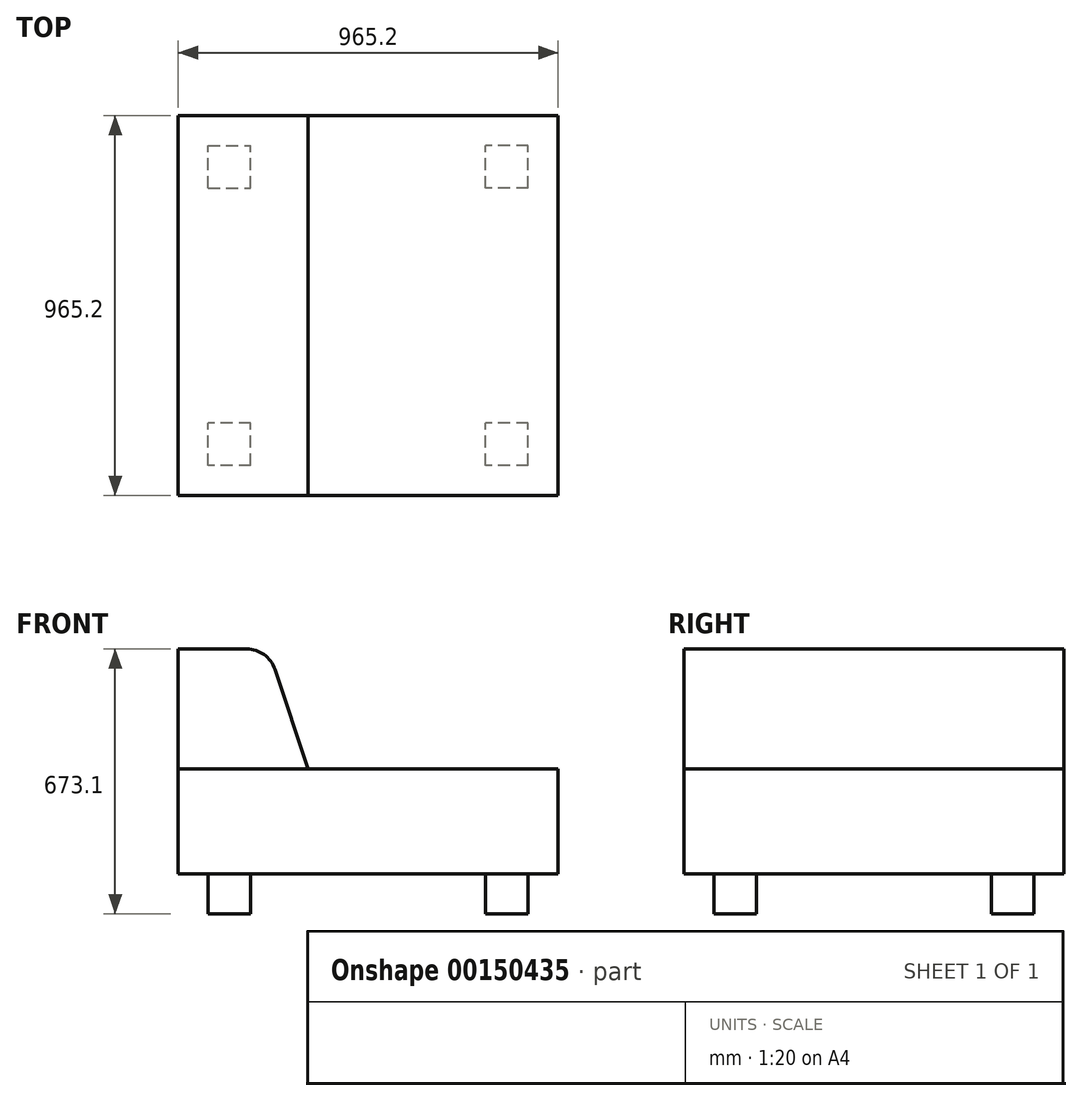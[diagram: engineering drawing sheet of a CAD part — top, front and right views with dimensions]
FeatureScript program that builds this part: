
annotation { "Feature Type Name" : "Feature", "Feature Type Description" : "" }
export const myFeature = defineFeature(function(context is Context, id is Id, definition is map)
    precondition{}
    {
        {
            var Q0;
            Q0=qCreatedBy(makeId("Top.planeOp"),FACE);
            var sketch = newSketch(context, id + "F0", { "sketchPlane" : qUnion([Q0])});
            skLineSegment(sketch, "E0.bottom", {"start": v(482.6, 482.6) * mm, "end": v(-482.6, 482.6) * mm});
            skLineSegment(sketch, "E0.top", {"start": v(482.6, -482.6) * mm, "end": v(-482.6, -482.6) * mm});
            skLineSegment(sketch, "E0.left", {"start": v(482.6, 482.6) * mm, "end": v(482.6, -482.6) * mm});
            skLineSegment(sketch, "E0.right", {"start": v(-482.6, 482.6) * mm, "end": v(-482.6, -482.6) * mm});
            skPoint(sketch, "E0.middle", {"position": v(0, 0) * mm});
            skSolve(sketch);
        }
        {
            var Q0;
            Q0 = qSketchRegion(id + "F0", true);
            extrude(context, id + "F1", {"entities" : qUnion([Q0]), "depth" : 266.7 * mm});
        }
        {
            var Q0;
            Q0=makeQuery(id+"F1.opExtrude","CAP_FACE",FACE,{"disambiguationData":[OSD([sQuery(id+"F0.wireOp",EDGE,"E0.bottom"),sQuery(id+"F0.wireOp",EDGE,"E0.top"),sQuery(id+"F0.wireOp",EDGE,"E0.left"),sQuery(id+"F0.wireOp",EDGE,"E0.right")])],"isStart":true});
            var sketch = newSketch(context, id + "F2", { "sketchPlane" : qUnion([Q0])});
            skLineSegment(sketch, "E1.bottom", {"start": v(352.43, 352.43) * mm, "end": v(-352.43, 352.43) * mm, "construction": true});
            skLineSegment(sketch, "E1.top", {"start": v(352.43, -352.43) * mm, "end": v(-352.43, -352.43) * mm, "construction": true});
            skLineSegment(sketch, "E1.left", {"start": v(352.43, 352.43) * mm, "end": v(352.43, -352.43) * mm, "construction": true});
            skLineSegment(sketch, "E1.right", {"start": v(-352.43, 352.43) * mm, "end": v(-352.43, -352.43) * mm, "construction": true});
            skPoint(sketch, "E1.middle", {"position": v(0, 0) * mm});
            skLineSegment(sketch, "E2.bottom", {"start": v(-298.45, 406.4) * mm, "end": v(-406.4, 406.4) * mm});
            skLineSegment(sketch, "E2.top", {"start": v(-298.45, 298.45) * mm, "end": v(-406.4, 298.45) * mm});
            skLineSegment(sketch, "E2.left", {"start": v(-298.45, 406.4) * mm, "end": v(-298.45, 298.45) * mm});
            skLineSegment(sketch, "E2.right", {"start": v(-406.4, 406.4) * mm, "end": v(-406.4, 298.45) * mm});
            skPoint(sketch, "E2.middle", {"position": v(-352.43, 352.43) * mm});
            skLineSegment(sketch, "E3.bottom", {"start": v(406.4, 406.4) * mm, "end": v(298.45, 406.4) * mm});
            skLineSegment(sketch, "E3.top", {"start": v(406.4, 298.45) * mm, "end": v(298.45, 298.45) * mm});
            skLineSegment(sketch, "E3.left", {"start": v(406.4, 406.4) * mm, "end": v(406.4, 298.45) * mm});
            skLineSegment(sketch, "E3.right", {"start": v(298.45, 406.4) * mm, "end": v(298.45, 298.45) * mm});
            skPoint(sketch, "E3.middle", {"position": v(352.43, 352.43) * mm});
            skLineSegment(sketch, "E4.bottom", {"start": v(406.4, -298.45) * mm, "end": v(298.45, -298.45) * mm});
            skLineSegment(sketch, "E4.top", {"start": v(406.4, -406.4) * mm, "end": v(298.45, -406.4) * mm});
            skLineSegment(sketch, "E4.left", {"start": v(406.4, -298.45) * mm, "end": v(406.4, -406.4) * mm});
            skLineSegment(sketch, "E4.right", {"start": v(298.45, -298.45) * mm, "end": v(298.45, -406.4) * mm});
            skPoint(sketch, "E4.middle", {"position": v(352.43, -352.43) * mm});
            skLineSegment(sketch, "E5.bottom", {"start": v(-406.4, -298.45) * mm, "end": v(-298.45, -298.45) * mm});
            skLineSegment(sketch, "E5.top", {"start": v(-406.4, -406.4) * mm, "end": v(-298.45, -406.4) * mm});
            skLineSegment(sketch, "E5.left", {"start": v(-406.4, -298.45) * mm, "end": v(-406.4, -406.4) * mm});
            skLineSegment(sketch, "E5.right", {"start": v(-298.45, -298.45) * mm, "end": v(-298.45, -406.4) * mm});
            skPoint(sketch, "E5.middle", {"position": v(-352.43, -352.43) * mm});
            skSolve(sketch);
        }
        {
            var Q0;
            Q0 = qSketchRegion(id + "F2", true);
            extrude(context, id + "F3", {"entities" : qUnion([Q0]), "operationType" : NewBodyOperationType.ADD, "depth" : 101.6 * mm});
        }
        {
            var Q0;
            Q0=makeQuery(id+"F1.opExtrude","SWEPT_FACE",FACE,{"disambiguationData":[OSD([sQuery(id+"F0.wireOp",EDGE,"E0.top")])]});
            var sketch = newSketch(context, id + "F4", { "sketchPlane" : qUnion([Q0])});
            skLineSegment(sketch, "E6", {"start": v(-482.6, 266.7) * mm, "end": v(-152.4, 266.7) * mm});
            skLineSegment(sketch, "E7", {"start": v(-152.4, 266.7) * mm, "end": v(-236.63, 519.4) * mm});
            skLineSegment(sketch, "E8", {"start": v(-308.92, 571.5) * mm, "end": v(-482.6, 571.5) * mm});
            skLineSegment(sketch, "E9", {"start": v(-482.6, 571.5) * mm, "end": v(-482.6, 266.7) * mm});
            skPoint(sketch, "E10.visualSharp", {"position": v(-254, 571.5) * mm});
            skArc(sketch, "E10.filletArc", {"start": v(-236.63, 519.4) * mm, "mid": v(-264.37, 557.12) * mm, "end": v(-308.92, 571.5) * mm});
            skSolve(sketch);
        }
        {
            var Q0;
            Q0 = qSketchRegion(id + "F4", true);
            var Q1;
            Q1=makeQuery(id+"F1.opExtrude","SWEPT_FACE",FACE,{"disambiguationData":[OSD([sQuery(id+"F0.wireOp",EDGE,"E0.bottom")])]});
            extrude(context, id + "F5", {"entities" : qUnion([Q0]), "endBound" : BoundingType.UP_TO_SURFACE, "oppositeDirection" : true, "endBoundEntityFace" : qUnion([Q1]), "depth" : 30.48 * mm});
        }
    });
